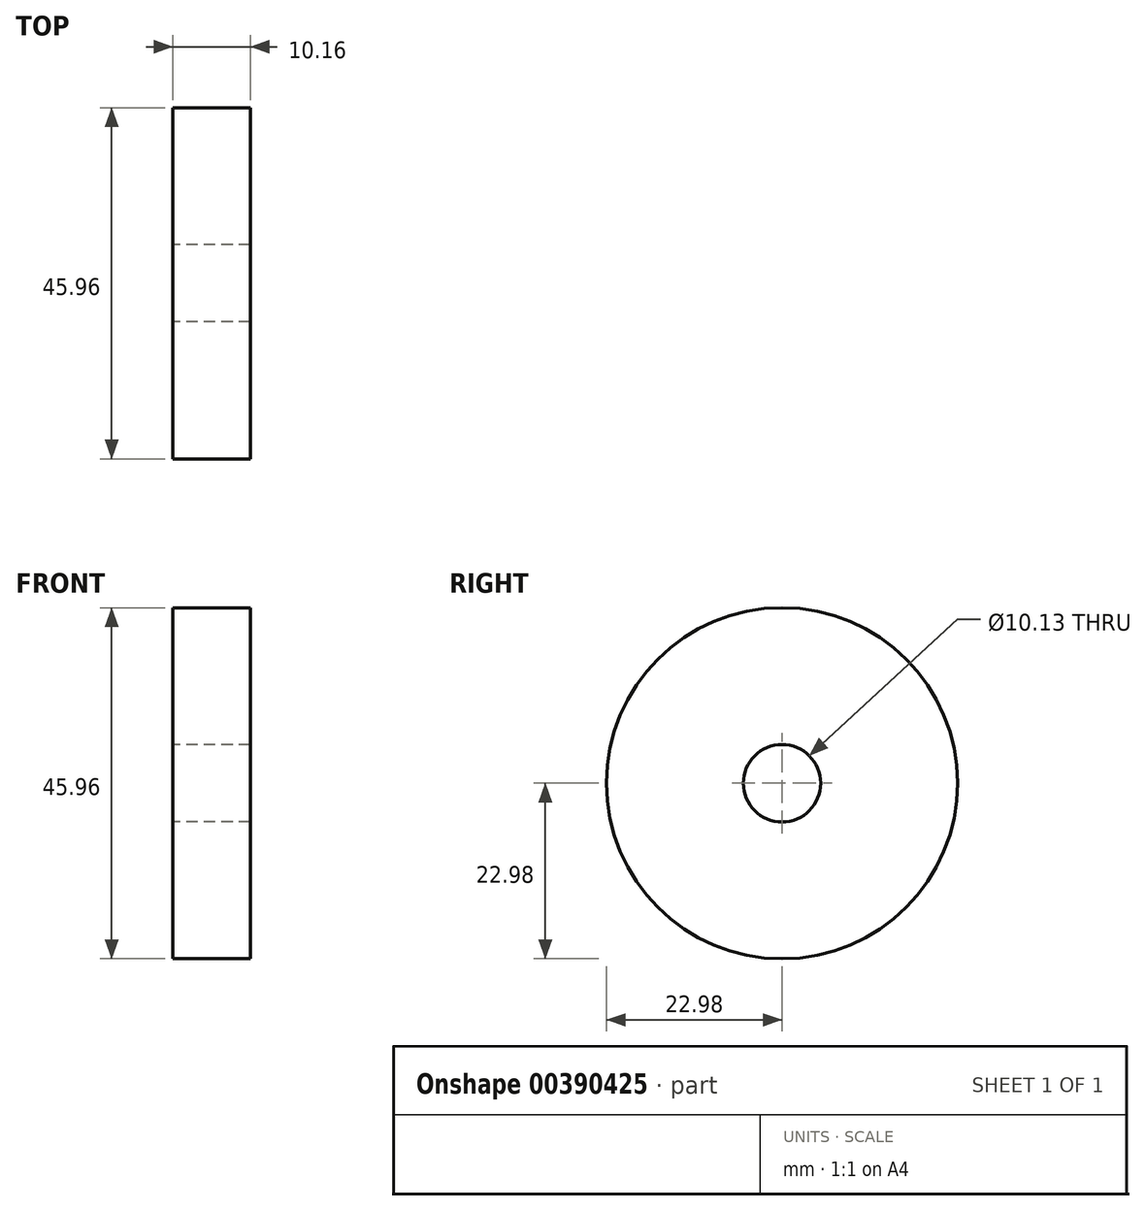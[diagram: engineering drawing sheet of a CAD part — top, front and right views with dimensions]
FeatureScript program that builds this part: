
annotation { "Feature Type Name" : "Feature", "Feature Type Description" : "" }
export const myFeature = defineFeature(function(context is Context, id is Id, definition is map)
    precondition{}
    {
        {
            var Q0;
            Q0=qCreatedBy(makeId("Right.planeOp"),FACE);
            var sketch = newSketch(context, id + "F0", { "sketchPlane" : qUnion([Q0])});
            skCircle(sketch, "E0", {"center": v(0, 0) * mm, "radius": 22.98 * mm});
            skCircle(sketch, "E1", {"center": v(0, 0) * mm, "radius": 5.06 * mm});
            skSolve(sketch);
        }
        {
            var Q0;
            Q0=makeQuery(id+"F0.imprint","IMPRINT",FACE,{"disambiguationData":[TD([[makeQuery(id+"F0.imprint","IMPRINT",EDGE,{"derivedFrom":sQuery(id+"F0.wireOp",EDGE,"E0")}),1.0]])]});
            extrude(context, id + "F1", {"entities" : qUnion([Q0]), "depth" : 10.16 * mm});
        }
    });
